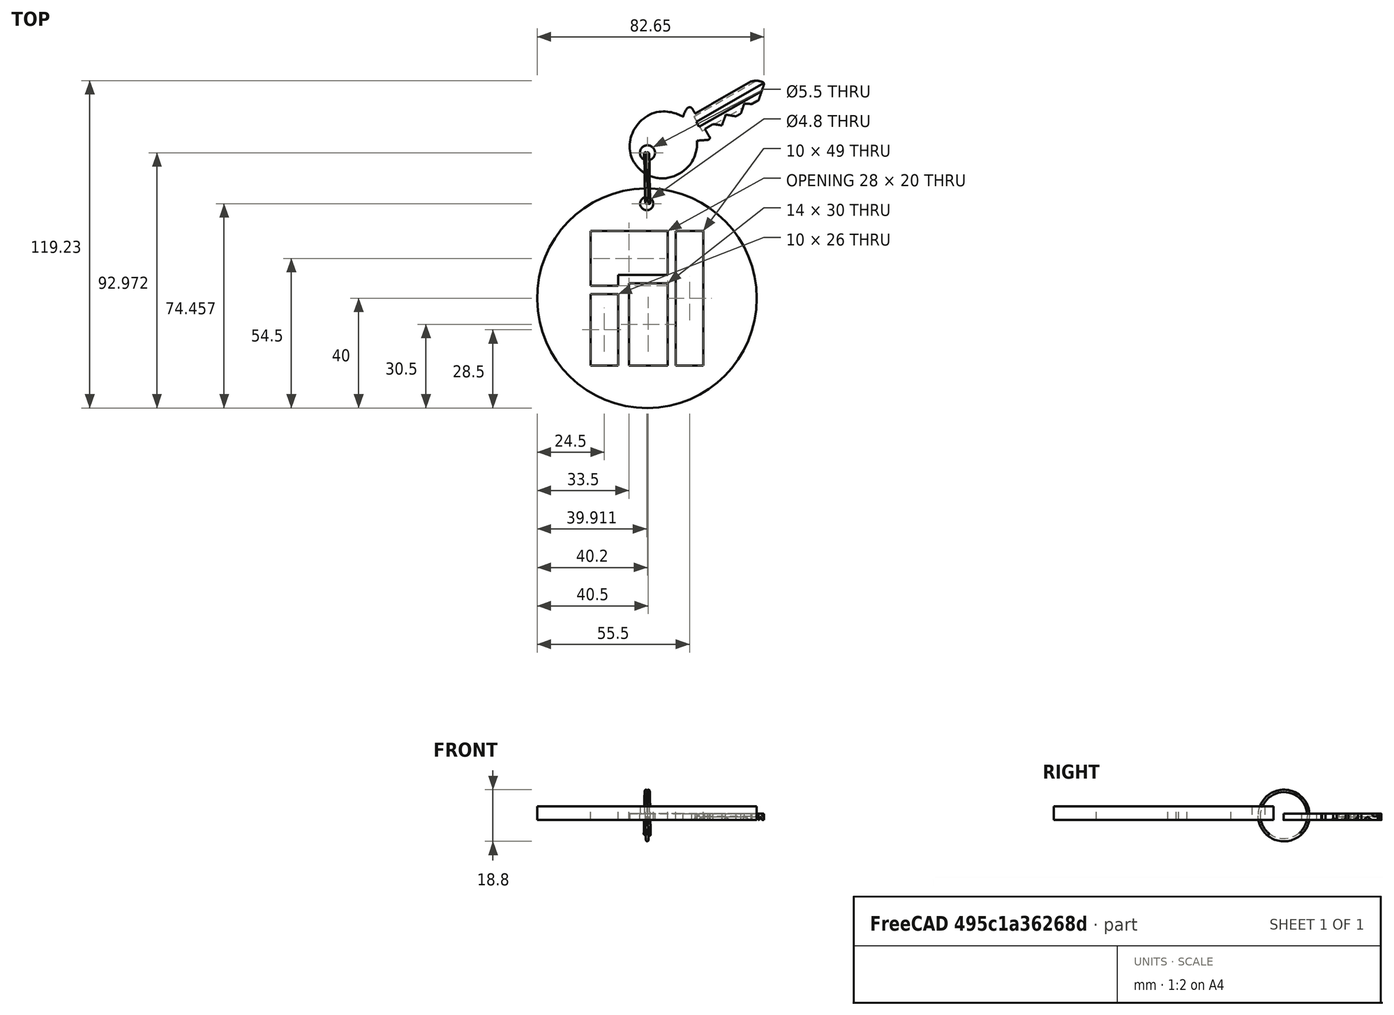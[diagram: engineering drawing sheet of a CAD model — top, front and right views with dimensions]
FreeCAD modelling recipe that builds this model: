
FCSTD DOCUMENT  (FreeCAD 0.16RUnknown)
Label: Llavero Manjaro1
License: CreativeCommons Attribution-ShareAlike
LicenseURL: http://creativecommons.org/licenses/by-sa/4.0/
objects: Part::Feature×2, Sketcher::SketchObject×1, PartDesign::Pad×1, App::DocumentObjectGroup×1
note: 5 computed .brp shape members not serialized (recipe doc carries the construction recipe); baked Part::Feature solids carry a one-line shape summary decoded from their .brp

FEATURE [Part::Feature] Sweep  label="key-ring-model-1"
  Placement = pos=(-1.2,30.2546,1.6391) rot=(0.333333,0.881918,0.333333;1.69612rad)
  shape: bbox 3.31 x 27.02 x 26.33 mm, 4 faces (baked)
FEATURE [Part::Feature] Cut  label="key-model-1"
  Placement = pos=(-5.46976,36.5266,0) rot=(0,0,1;0.517888rad)
  shape: bbox 49.82 x 36.6 x 2.3 mm, 44 faces (baked)
FEATURE [Sketcher::SketchObject] Sketch
  Placement = pos=(-21,-38,0) rot=(0,0,1;0rad)
  sketch-geometry (27):
    g0: LineSegment StartX=0 StartY=0 StartZ=0 EndX=0 EndY=26 EndZ=0
    g1: LineSegment StartX=0 StartY=26 StartZ=0 EndX=10 EndY=26 EndZ=0
    g2: LineSegment StartX=10 StartY=26 StartZ=0 EndX=10 EndY=0 EndZ=0
    g3: LineSegment StartX=10 StartY=0 StartZ=0 EndX=0 EndY=0 EndZ=0
    g4: LineSegment StartX=0 StartY=29 StartZ=0 EndX=0 EndY=49 EndZ=0
    g5: LineSegment StartX=0 StartY=49 StartZ=0 EndX=28 EndY=49 EndZ=0
    g6: LineSegment StartX=28 StartY=49 StartZ=0 EndX=28 EndY=33 EndZ=0
    g7: LineSegment StartX=28 StartY=33 StartZ=0 EndX=10 EndY=33 EndZ=0
    g8: LineSegment StartX=10 StartY=33 StartZ=0 EndX=10 EndY=29 EndZ=0
    g9: LineSegment StartX=10 StartY=29 StartZ=0 EndX=0 EndY=29 EndZ=0
    g10: LineSegment StartX=14 StartY=30 StartZ=0 EndX=28 EndY=30 EndZ=0
    g11: LineSegment StartX=28 StartY=30 StartZ=0 EndX=28 EndY=0 EndZ=0
    g12: LineSegment StartX=28 StartY=0 StartZ=0 EndX=14 EndY=0 EndZ=0
    g13: LineSegment StartX=14 StartY=0 StartZ=0 EndX=14 EndY=30 EndZ=0
    g14: LineSegment StartX=31 StartY=49 StartZ=0 EndX=41 EndY=49 EndZ=0
    g15: LineSegment StartX=41 StartY=49 StartZ=0 EndX=41 EndY=0 EndZ=0
    g16: LineSegment StartX=41 StartY=0 StartZ=0 EndX=31 EndY=0 EndZ=0
    g17: LineSegment StartX=31 StartY=0 StartZ=0 EndX=31 EndY=49 EndZ=0
    g18: LineSegment [constr] StartX=28 StartY=49 StartZ=0 EndX=31 EndY=49 EndZ=0
    g19: LineSegment [constr] StartX=28 StartY=33 StartZ=0 EndX=28 EndY=30 EndZ=0
    g20: LineSegment [constr] StartX=20.5 StartY=49 StartZ=0 EndX=20.5 EndY=24.5 EndZ=0
    g21: LineSegment [constr] StartX=20.5 StartY=24.5 StartZ=0 EndX=20.5 EndY=0 EndZ=0
    g22: LineSegment [constr] StartX=0 StartY=24.5 StartZ=0 EndX=20.5 EndY=24.5 EndZ=0
    g23: LineSegment [constr] StartX=20.5 StartY=24.5 StartZ=0 EndX=41 EndY=24.5 EndZ=0
    g24: Circle CenterX=20.5 CenterY=24.5 CenterZ=0 NormalX=0 NormalY=0 NormalZ=1 Radius=40
    g25: Circle CenterX=20.411 CenterY=58.9566 CenterZ=0 NormalX=0 NormalY=0 NormalZ=1 Radius=2.39787
    g26: LineSegment [constr] StartX=20.5 StartY=48.9566 StartZ=0 EndX=20.411 EndY=58.9566 EndZ=0
  constraints (75):
    c: Coincident(g0,g1)
    c: Vertical(g0)
    c: Horizontal(g1)
    c: Vertical(g2)
    c: Coincident(g3,g0)
    c: DistanceY(g0,g0) = 26
    c: Coincident(g4,g9)
    c: Horizontal(g9)
    c: DistanceY(g0,g4) = 3
    c: DistanceY(g4,g4) = 20
    c: Coincident(g5,g6)
    c: Vertical(g6)
    c: Coincident(g6,g7)
    c: Horizontal(g7)
    c: DistanceX(g5,g5) = 28
    c: Horizontal(g5)
    c: Coincident(g7,g8)
    c: Vertical(g8)
    c: Coincident(g9,g8)
    c: Vertical(g4)
    c: PointOnObject(g4,g-2)
    c: PointOnObject(g0,g-2)
    c: PointOnObject(g0,g-1)
    c: Coincident(g4,g5)
    c: Coincident(g10,g11)
    c: Coincident(g11,g12)
    c: Coincident(g12,g13)
    c: Coincident(g13,g10)
    c: Horizontal(g10)
    c: Horizontal(g12)
    c: Vertical(g11)
    c: Vertical(g13)
    c: Horizontal(g3)
    c: Coincident(g1,g2)
    c: Equal(g1,g9)
    c: PointOnObject(g12,g-1)
    c: DistanceX(g3,g12) = 4
    c: Coincident(g14,g15)
    c: Coincident(g15,g16)
    c: Coincident(g16,g17)
    c: Coincident(g17,g14)
    c: Horizontal(g14)
    c: Horizontal(g16)
    c: Vertical(g17)
    c: PointOnObject(g15,g-1)
    c: DistanceX(g14,g14) = 10
    c: Horizontal(g18)
    c: Coincident(g18,g14)
    c: Coincident(g18,g5)
    c: DistanceX(g18,g18) = 3
    c: DistanceY(g13,g13) = 30
    c: Vertical(g19)
    c: Coincident(g10,g19)
    c: Coincident(g6,g19)
    c: Coincident(g2,g3)
    c: Vertical(g15)
    c: DistanceX(g9,g9) = 10
    c: Coincident(g20,g21)
    c: PointOnObject(g20,g5)
    c: Vertical(g20)
    c: Equal(g20,g21)
    c: Vertical(g21)
    c: Coincident(g22,g23)
    c: Equal(g23,g22)
    c: Coincident(g20,g22)
    c: PointOnObject(g23,g15)
    c: PointOnObject(g22,g0)
    c: Horizontal(g23)
    c: Horizontal(g22)
    c: PointOnObject(g21,g12)
    c: Radius(g24) = 40
    c: DistanceY(g19,g19) = 3
    c: Coincident(g24,g20)
    c: Coincident(g25,g26)
    c: DistanceY(g26,g26) = 10
FEATURE [PartDesign::Pad] Pad
  Length = 5
  Length2 = 100
  Placement = pos=(-21,-38,0) rot=(0,0,1;0rad)
  Sketch = -> Sketch
  Type = 0
FEATURE [App::DocumentObjectGroup] Group  label="Assembly"
  Group = -> [Sweep,Cut,Pad]
